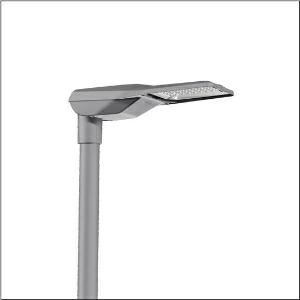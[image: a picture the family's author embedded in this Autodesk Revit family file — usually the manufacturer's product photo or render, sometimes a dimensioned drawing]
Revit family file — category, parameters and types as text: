
# Revit family: streetlight_sl_21_iq_mini___stw1_0a_5xe2e31g08jb_fb58
name_source: partatom
category: Lighting Fixtures
units: mm (PartAtom-declared; Revit-internal decimal feet)

## family parameters
Cut with Voids When Loaded = No
Host = Face
Light Source = No
Part Type = Normal
Room Calculation Point = No
Round Connector Dimension = Use Diameter
Shared = No

## types (1)
- --- (1 x LED, 10820 lm, 71.6 W, 3000K)
    Apparent Load = 72 VA
    CIE Flux Codes = 39 75 98 100 100
    Color Rendering = 70
    Color Temperature = 3000K
    Default Elevation = 1800 mm
    Description = Streetlight SL 21 iQ mini, mast luminaire, primary light control with lens, of PMMA, primary optical cover: cover, of toughened safety glass, transparent, light distribution: STW1.0a, light emission: direct distribution, primary light characteristic: asymmetric, installation type: post-top, side-entry, LED, High Power LED, rated luminous flux: 10.820lm, luminous efficacy: 151lm/W, light colour: 730, colour temperature: 3000K, control: Street-Remote, Auto-Match, Temp-Guard, Lumen-Switch, Night-Set, Smart-Wire, Light-Fading, Desk-Remote (wireless, voltage-free reading and setting of iQ features in the workshop via application-optimized NFC function/RFID function), optimised constant luminous flux control (CLO 2.0), presetting dimming linear, mains connection: 220..240V, AC, 50/60Hz, start of lifetime: 72W, end of service life: 75W, reduction: 33W, luminaire housing, of diecast aluminium, powder-coated, Siteco® metallic grey (DB 702S), corrosivity category C5 mid according to DIN EN ISO 12944, please order mast flange separately, inclination adjustable: 0°, 5°, 10°, 15°, sealing non-destructively replaceable, multi-level sealing system, length: 628mm, width: 235mm, height: 110mm, mast flange for spigot size: 42mm (side-entry): 5XC10008XM4, 60/48mm (side-entry/post-top): 5XC10108XM2, 76/60mm (side-entry/post-top): 5XC10108XM1, protection rating (complete): IP66, insulation class (complete): insulation class II (safety insulation), certification: CE, ENEC, ENEC+, VDE, impact resistance: IK09, permissible operating ambient temperature for outdoor applications: -40..+50°C, standard-compliant lighting for roads and squares, packaging unit: 1 piece

Light Distribution: STW1.0a
    Height = 110 mm
    Lamp = 1 x LED
    Lamp Light Flux = 10820 lm
    Lamp Power = 71.6 W
    Lamp count = 1
    Length = 625 mm
    Luminous efficacy = 151 lm/W
    Manufacturer = Siteco
    ModVariant = No
    Model = 5XE2E31G08JB
    Number of Poles = 1
    OnlyDefault = Yes
    Power Factor = 1
    Product Name = Streetlight SL 21 iQ mini | STW1.0a
    Product group = mast luminaire | pylon top
    ProductGroupID = 6100
    Protection Class = Protection class II
    Protection Degree = IP 66
    RLX_Detail_Level = 1
    RLX_Emergency_Light_Flux = 0 lm
    RLX_Emergency_Type = 0
    RLX_Emergency_Type_DB = No
    RlxData = <blob elided: 92221 chars, md5=1a83fe27>
    Socket = socket
    Standby Power = 0 W
    System Light Flux = 10820 lm
    System Power = 72 W
    Type Comments = factory setting: luminous flux: 100 % | dim-lin: 254 | 746 mA
    Type Image = l_1003519.jpg
    URL = http://relux.com
    VarID = @adj_102929
    Voltage = 0 V
    Weight = 0.00 kg
    Width = 234 mm

## geometry (parser evidence)
native form markers: Blend x4, Sweep x12
no freeform markers — native parametric forms only
